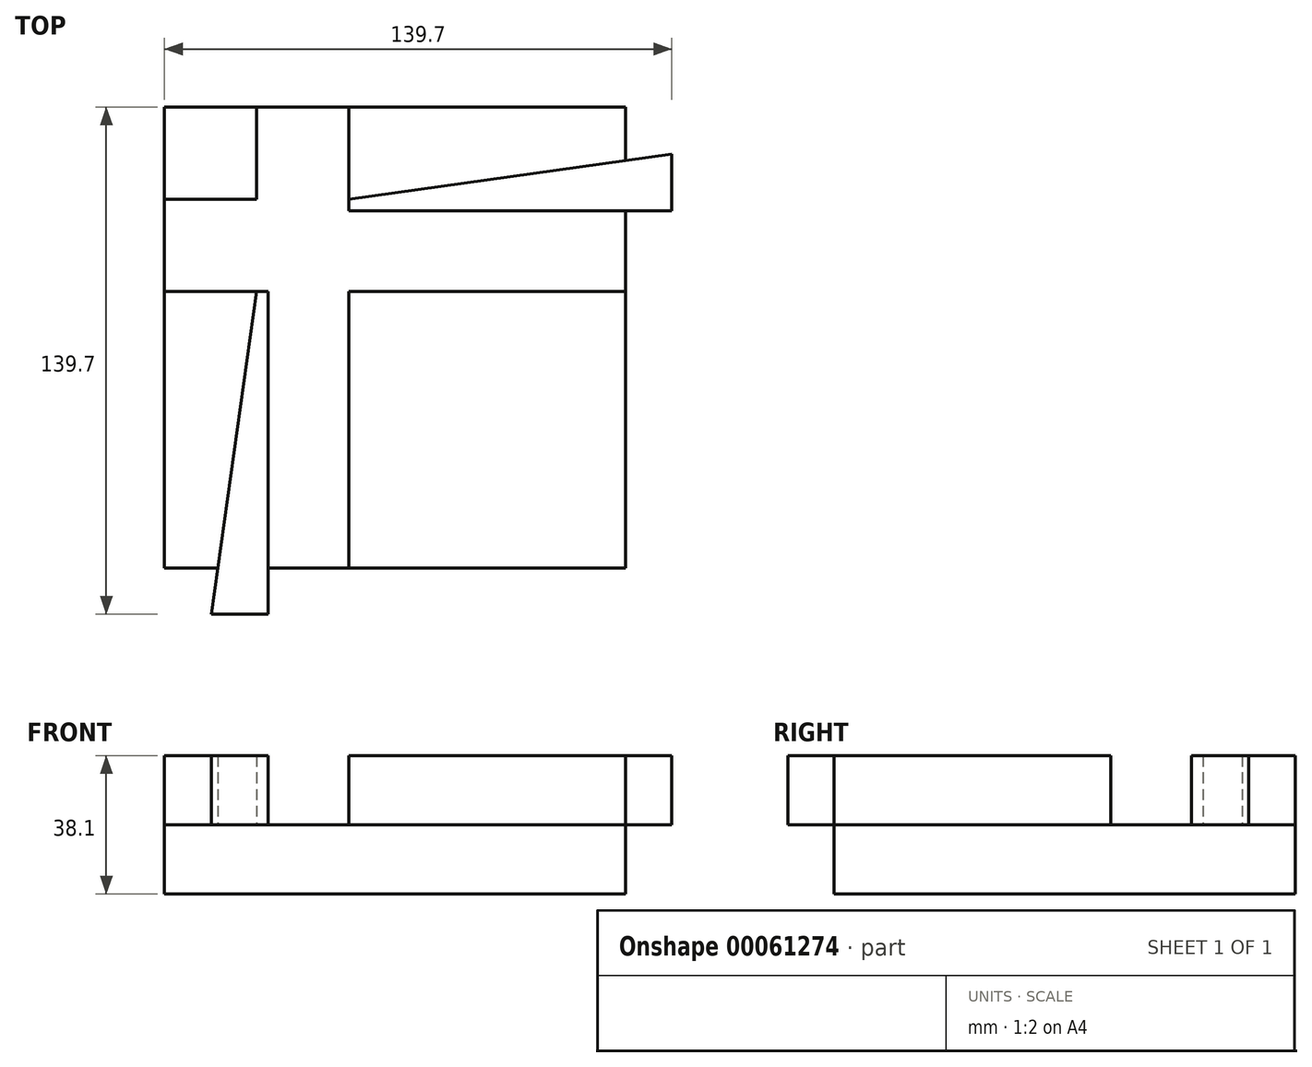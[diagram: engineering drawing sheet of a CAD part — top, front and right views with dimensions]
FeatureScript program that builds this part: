
annotation { "Feature Type Name" : "Feature", "Feature Type Description" : "" }
export const myFeature = defineFeature(function(context is Context, id is Id, definition is map)
    precondition{}
    {
        {
            var Q0;
            Q0=qCreatedBy(makeId("Top.planeOp"),FACE);
            var sketch = newSketch(context, id + "F0", { "sketchPlane" : qUnion([Q0])});
            skLineSegment(sketch, "E0.bottom", {"start": v(0, 0) * mm, "end": v(127, 0) * mm});
            skLineSegment(sketch, "E0.top", {"start": v(0, -127) * mm, "end": v(127, -127) * mm});
            skLineSegment(sketch, "E0.left", {"start": v(0, 0) * mm, "end": v(0, -127) * mm});
            skLineSegment(sketch, "E0.right", {"start": v(127, 0) * mm, "end": v(127, -127) * mm});
            skSolve(sketch);
        }
        {
            var Q0;
            Q0=makeQuery(id+"F0.imprint","IMPRINT",FACE,{"disambiguationData":[TD([[makeQuery(id+"F0.imprint","IMPRINT",EDGE,{"derivedFrom":sQuery(id+"F0.wireOp",EDGE,"E0.bottom")}),-1.0]])]});
            extrude(context, id + "F1", {"entities" : qUnion([Q0]), "depth" : 19.05 * mm});
        }
        {
            var Q0;
            Q0=makeQuery(id+"F1.opExtrude","CAP_FACE",FACE,{"disambiguationData":[OSD([sQuery(id+"F0.wireOp",EDGE,"E0.bottom"),sQuery(id+"F0.wireOp",EDGE,"E0.top"),sQuery(id+"F0.wireOp",EDGE,"E0.left"),sQuery(id+"F0.wireOp",EDGE,"E0.right")])],"isStart":false});
            var sketch = newSketch(context, id + "F2", { "sketchPlane" : qUnion([Q0])});
            skLineSegment(sketch, "E1.bottom", {"start": v(0, 0) * mm, "end": v(25.4, 0) * mm});
            skLineSegment(sketch, "E1.top", {"start": v(0, -25.4) * mm, "end": v(25.4, -25.4) * mm});
            skLineSegment(sketch, "E1.left", {"start": v(0, 0) * mm, "end": v(0, -25.4) * mm});
            skLineSegment(sketch, "E1.right", {"start": v(25.4, 0) * mm, "end": v(25.4, -25.4) * mm});
            skLineSegment(sketch, "E2.bottom", {"start": v(0, -127) * mm, "end": v(25.4, -127) * mm});
            skLineSegment(sketch, "E2.top", {"start": v(0, -50.8) * mm, "end": v(25.4, -50.8) * mm});
            skLineSegment(sketch, "E2.left", {"start": v(0, -127) * mm, "end": v(0, -50.8) * mm});
            skLineSegment(sketch, "E2.right", {"start": v(25.4, -127) * mm, "end": v(25.4, -50.8) * mm, "construction": true});
            skLineSegment(sketch, "E3.bottom", {"start": v(127, 0) * mm, "end": v(50.8, 0) * mm});
            skLineSegment(sketch, "E3.top", {"start": v(127, -25.4) * mm, "end": v(50.8, -25.4) * mm, "construction": true});
            skLineSegment(sketch, "E3.left", {"start": v(127, 0) * mm, "end": v(127, -25.4) * mm});
            skLineSegment(sketch, "E3.right", {"start": v(50.8, 0) * mm, "end": v(50.8, -25.4) * mm});
            skLineSegment(sketch, "E4.bottom", {"start": v(127, -127) * mm, "end": v(50.8, -127) * mm});
            skLineSegment(sketch, "E4.top", {"start": v(127, -50.8) * mm, "end": v(50.8, -50.8) * mm});
            skLineSegment(sketch, "E4.left", {"start": v(127, -127) * mm, "end": v(127, -50.8) * mm});
            skLineSegment(sketch, "E4.right", {"start": v(50.8, -127) * mm, "end": v(50.8, -50.8) * mm});
            skLineSegment(sketch, "E5", {"start": v(50.8, -25.4) * mm, "end": v(127, -14.7) * mm});
            skLineSegment(sketch, "E6", {"start": v(25.4, -50.8) * mm, "end": v(14.7, -127) * mm});
            skSolve(sketch);
        }
        {
            var Q0;
            Q0=makeQuery(id+"F2.imprint","IMPRINT",FACE,{"disambiguationData":[TD([[makeQuery(id+"F2.imprint","IMPRINT",EDGE,{"derivedFrom":sQuery(id+"F2.wireOp",EDGE,"E3.bottom")}),-1.0]])]});
            var Q1;
            Q1=makeQuery(id+"F2.imprint","IMPRINT",FACE,{"disambiguationData":[TD([[makeQuery(id+"F2.imprint","IMPRINT",EDGE,{"derivedFrom":sQuery(id+"F2.wireOp",EDGE,"E2.bottom")}),1.0]])]});
            var Q2;
            Q2=makeQuery(id+"F2.imprint","IMPRINT",FACE,{"disambiguationData":[TD([[makeQuery(id+"F2.imprint","IMPRINT",EDGE,{"derivedFrom":sQuery(id+"F2.wireOp",EDGE,"E1.bottom")}),-1.0]])]});
            var Q3;
            Q3=makeQuery(id+"F2.imprint","IMPRINT",FACE,{"disambiguationData":[TD([[makeQuery(id+"F2.imprint","IMPRINT",EDGE,{"derivedFrom":sQuery(id+"F2.wireOp",EDGE,"E4.bottom")}),1.0]])]});
            extrude(context, id + "F3", {"entities" : qUnion([Q0, Q1, Q2, Q3]), "depth" : 19.05 * mm});
        }
        {
            var Q0;
            Q0=makeQuery(id+"F1.opExtrude","CAP_FACE",FACE,{"disambiguationData":[OSD([sQuery(id+"F0.wireOp",EDGE,"E0.bottom"),sQuery(id+"F0.wireOp",EDGE,"E0.top"),sQuery(id+"F0.wireOp",EDGE,"E0.left"),sQuery(id+"F0.wireOp",EDGE,"E0.right")])],"isStart":false});
            var sketch = newSketch(context, id + "F4", { "sketchPlane" : qUnion([Q0])});
            skLineSegment(sketch, "E7.0", {"start": v(0, -50.8) * mm, "end": v(25.4, -50.8) * mm});
            skLineSegment(sketch, "E8.0", {"start": v(25.4, -50.8) * mm, "end": v(14.7, -127) * mm});
            skLineSegment(sketch, "E9.bottom", {"start": v(25.4, -50.8) * mm, "end": v(28.58, -50.8) * mm});
            skLineSegment(sketch, "E9.top", {"start": v(25.4, -127) * mm, "end": v(28.58, -127) * mm});
            skLineSegment(sketch, "E9.left", {"start": v(25.4, -50.8) * mm, "end": v(25.4, -127) * mm, "construction": true});
            skLineSegment(sketch, "E9.right", {"start": v(28.58, -50.8) * mm, "end": v(28.58, -127) * mm});
            skLineSegment(sketch, "E10.0", {"start": v(50.8, 0) * mm, "end": v(50.8, -25.4) * mm});
            skLineSegment(sketch, "E10.1", {"start": v(50.8, -25.4) * mm, "end": v(127, -14.7) * mm});
            skLineSegment(sketch, "E11.bottom", {"start": v(50.8, -25.4) * mm, "end": v(127, -25.4) * mm, "construction": true});
            skLineSegment(sketch, "E11.top", {"start": v(50.8, -28.57) * mm, "end": v(127, -28.57) * mm});
            skLineSegment(sketch, "E11.left", {"start": v(50.8, -25.4) * mm, "end": v(50.8, -28.57) * mm});
            skLineSegment(sketch, "E11.right", {"start": v(127, -25.4) * mm, "end": v(127, -28.57) * mm});
            skLineSegment(sketch, "E12", {"start": v(127, -14.7) * mm, "end": v(139.7, -12.9) * mm});
            skLineSegment(sketch, "E13", {"start": v(139.7, -12.9) * mm, "end": v(139.7, -28.57) * mm});
            skLineSegment(sketch, "E14", {"start": v(139.7, -28.57) * mm, "end": v(127, -28.57) * mm});
            skLineSegment(sketch, "E15", {"start": v(14.7, -127) * mm, "end": v(12.9, -139.7) * mm});
            skLineSegment(sketch, "E16", {"start": v(12.9, -139.7) * mm, "end": v(28.58, -139.7) * mm});
            skLineSegment(sketch, "E17", {"start": v(28.58, -139.7) * mm, "end": v(28.58, -127) * mm});
            skSolve(sketch);
        }
        {
            var Q0;
            {var subQ1=sQuery(id+"F4.wireOp",EDGE,"E10.1");Q0=makeQuery(id+"F4.imprint","IMPRINT",FACE,{"disambiguationData":[TD([[makeQuery(id+"F4.imprint","IMPRINT",EDGE,{"derivedFrom":subQ1}),-1.0]])]});}
            var Q1;
            {var subQ1=sQuery(id+"F4.wireOp",EDGE,"E8.0");Q1=makeQuery(id+"F4.imprint","IMPRINT",FACE,{"disambiguationData":[TD([[makeQuery(id+"F4.imprint","IMPRINT",EDGE,{"derivedFrom":subQ1}),1.0]])]});}
            var Q2;
            {var subQ1=sQuery(id+"F4.wireOp",EDGE,"E9.top");Q2=makeQuery(id+"F4.imprint","IMPRINT",FACE,{"disambiguationData":[TD([[makeQuery(id+"F4.imprint","IMPRINT",EDGE,{"derivedFrom":subQ1}),-1.0]])]});}
            var Q3;
            {var subQ2=sQuery(id+"F4.wireOp",EDGE,"E11.right");Q3=makeQuery(id+"F4.imprint","IMPRINT",FACE,{"disambiguationData":[TD([[makeQuery(id+"F4.imprint","IMPRINT",EDGE,{"derivedFrom":subQ2}),1.0]])]});}
            extrude(context, id + "F5", {"entities" : qUnion([Q0, Q1, Q2, Q3]), "depth" : 19.05 * mm});
        }
    });
